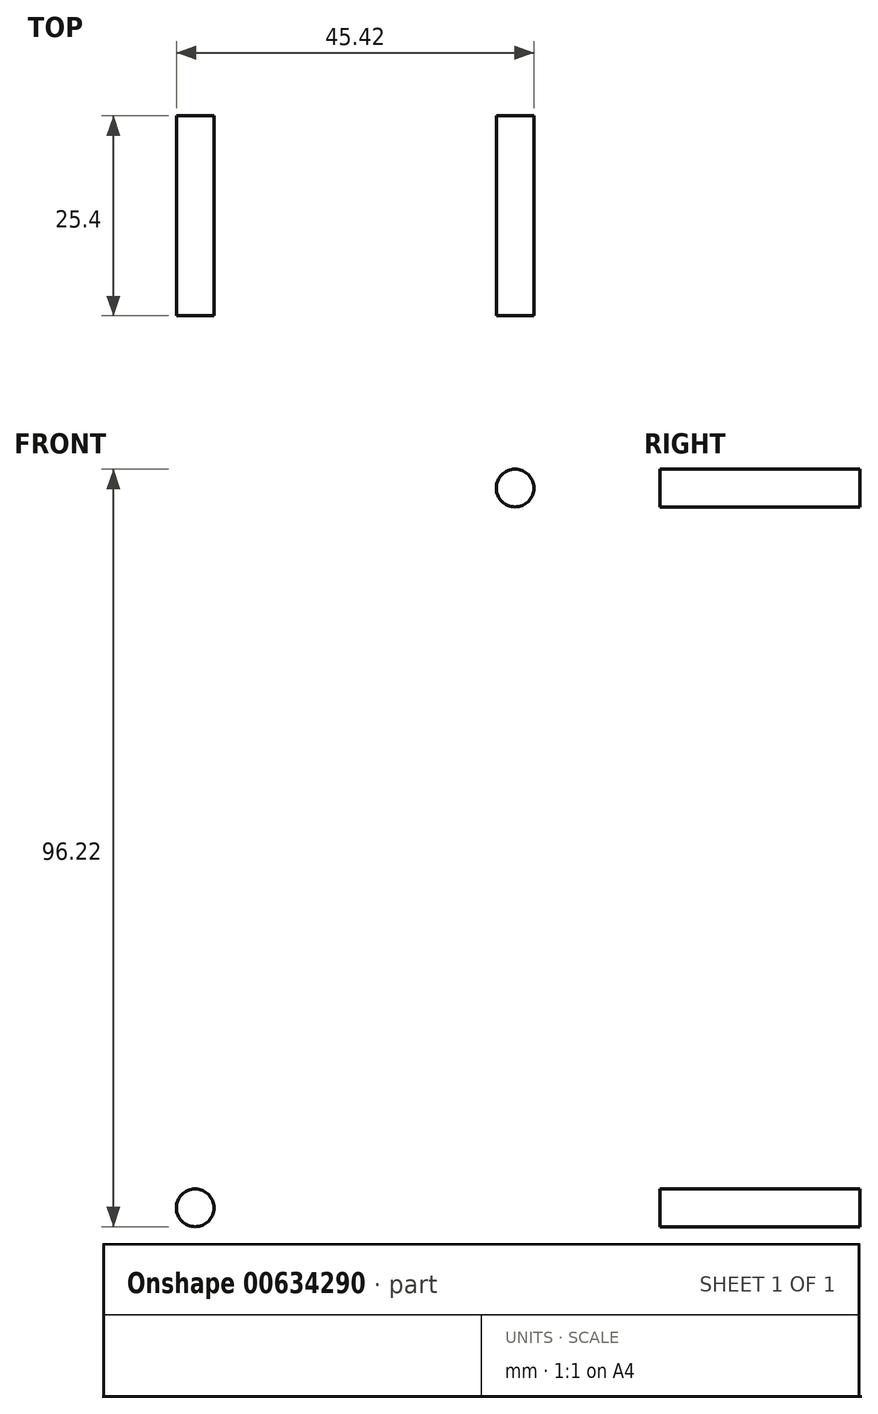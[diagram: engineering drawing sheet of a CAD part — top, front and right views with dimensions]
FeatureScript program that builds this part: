
annotation { "Feature Type Name" : "Feature", "Feature Type Description" : "" }
export const myFeature = defineFeature(function(context is Context, id is Id, definition is map)
    precondition{}
    {
        {
            var Q0;
            Q0=qCreatedBy(makeId("Front.planeOp"),FACE);
            var sketch = newSketch(context, id + "F0", { "sketchPlane" : qUnion([Q0])});
            skLineSegment(sketch, "E0.bottom", {"start": v(25.4, 50.8) * mm, "end": v(-25.4, 50.8) * mm});
            skLineSegment(sketch, "E0.top", {"start": v(25.4, -50.8) * mm, "end": v(-25.4, -50.8) * mm});
            skLineSegment(sketch, "E0.left", {"start": v(25.4, 50.8) * mm, "end": v(25.4, -50.8) * mm});
            skLineSegment(sketch, "E0.right", {"start": v(-25.4, 50.8) * mm, "end": v(-25.4, -50.8) * mm});
            skPoint(sketch, "E0.middle", {"position": v(0, 0) * mm});
            skCircle(sketch, "E1", {"center": v(0, -26.46) * mm, "radius": 7.62 * mm});
            skCircle(sketch, "E2.MirrorC", {"center": v(0, 26.46) * mm, "radius": 7.62 * mm});
            skSolve(sketch);
        }
        {
            var Q0;
            Q0=makeQuery(id+"F0.imprint","IMPRINT",FACE,{"disambiguationData":[TD([[makeQuery(id+"F0.imprint","IMPRINT",EDGE,{"derivedFrom":sQuery(id+"F0.wireOp",EDGE,"E0.bottom")}),1.0]])]});
            extrude(context, id + "F1", {"entities" : qUnion([Q0]), "endBound" : BoundingType.SYMMETRIC, "oppositeDirection" : true, "depth" : 25.4 * mm, "offsetDistance" : 25.4 * mm});
        }
        {
            var Q0;
            Q0=makeQuery(id+"F1.opExtrude","SWEPT_EDGE",EDGE,{"disambiguationData":[OSD([sQuery(id+"F0.wireOp",EDGE,"E0.bottom"),sQuery(id+"F0.wireOp",EDGE,"E0.right")])]});
            var Q1;
            Q1=makeQuery(id+"F1.opExtrude","SWEPT_EDGE",EDGE,{"disambiguationData":[OSD([sQuery(id+"F0.wireOp",EDGE,"E0.bottom"),sQuery(id+"F0.wireOp",EDGE,"E0.left")])]});
            var Q2;
            Q2=makeQuery(id+"F1.opExtrude","SWEPT_EDGE",EDGE,{"disambiguationData":[OSD([sQuery(id+"F0.wireOp",EDGE,"E0.top"),sQuery(id+"F0.wireOp",EDGE,"E0.left")])]});
            var Q3;
            Q3=makeQuery(id+"F1.opExtrude","SWEPT_EDGE",EDGE,{"disambiguationData":[OSD([sQuery(id+"F0.wireOp",EDGE,"E0.top"),sQuery(id+"F0.wireOp",EDGE,"E0.right")])]});
            fillet(context, id + "F2", {"entities" : qUnion([Q0, Q1, Q2, Q3]), "radius" : 5.08 * mm, "tangentPropagation" : true, "allowEdgeOverflow" : false});
        }
        {
            var Q0;
            Q0=makeQuery(id+"F1.opExtrude","CAP_FACE",FACE,{"disambiguationData":[OSD([sQuery(id+"F0.wireOp",EDGE,"E0.bottom"),sQuery(id+"F0.wireOp",EDGE,"E0.top"),sQuery(id+"F0.wireOp",EDGE,"E0.left"),sQuery(id+"F0.wireOp",EDGE,"E0.right"),sQuery(id+"F0.wireOp",EDGE,"E1"),sQuery(id+"F0.wireOp",EDGE,"E2.MirrorC")])],"isStart":true});
            var sketch = newSketch(context, id + "F3", { "sketchPlane" : qUnion([Q0])});
            skCircle(sketch, "E3", {"center": v(-20.32, 45.72) * mm, "radius": 2.4 * mm});
            skCircle(sketch, "E4.MirrorC", {"center": v(20.32, 45.72) * mm, "radius": 2.4 * mm});
            skCircle(sketch, "E5.MirrorC", {"center": v(20.32, -45.72) * mm, "radius": 2.4 * mm});
            skCircle(sketch, "E6.MirrorC", {"center": v(-20.32, -45.72) * mm, "radius": 2.4 * mm});
            skSolve(sketch);
        }
        {
            var Q0;
            Q0=makeQuery(id+"F3.imprint","IMPRINT",FACE,{"disambiguationData":[TD([[makeQuery(id+"F3.imprint","IMPRINT",EDGE,{"derivedFrom":sQuery(id+"F3.wireOp",EDGE,"E3")}),1.0]])]});
            var Q1;
            Q1=makeQuery(id+"F3.imprint","IMPRINT",FACE,{"disambiguationData":[TD([[makeQuery(id+"F3.imprint","IMPRINT",EDGE,{"derivedFrom":sQuery(id+"F3.wireOp",EDGE,"E4.MirrorC")}),-1.0]])]});
            var Q2;
            Q2=makeQuery(id+"F3.imprint","IMPRINT",FACE,{"disambiguationData":[TD([[makeQuery(id+"F3.imprint","IMPRINT",EDGE,{"derivedFrom":sQuery(id+"F3.wireOp",EDGE,"E5.MirrorC")}),1.0]])]});
            var Q3;
            Q3=makeQuery(id+"F3.imprint","IMPRINT",FACE,{"disambiguationData":[TD([[makeQuery(id+"F3.imprint","IMPRINT",EDGE,{"derivedFrom":sQuery(id+"F3.wireOp",EDGE,"E6.MirrorC")}),-1.0]])]});
            extrude(context, id + "F4", {"entities" : qUnion([Q0, Q1, Q2, Q3]), "operationType" : NewBodyOperationType.REMOVE, "endBound" : BoundingType.SYMMETRIC, "oppositeDirection" : true, "depth" : 144.78 * mm, "offsetDistance" : 25.4 * mm});
        }
    });
